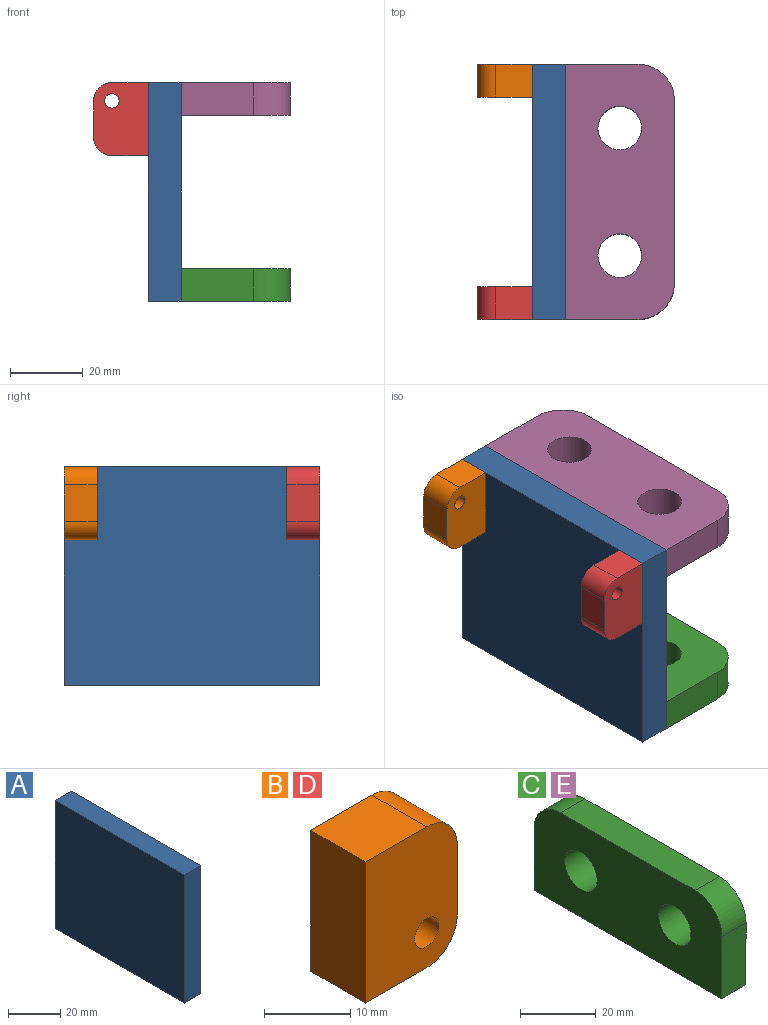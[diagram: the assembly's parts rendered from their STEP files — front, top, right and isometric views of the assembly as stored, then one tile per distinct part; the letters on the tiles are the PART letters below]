
ASSEMBLY  parts=5 mates=12
PART A: 6 faces, bbox 9x70x60 mm
  f0: plane 70x60mm, normal (1,0,0), area 4200mm2, adj f1,f2,f4,f5
  f1: plane 70x9mm, normal (0,0,1), area 630mm2, adj f0,f3,f4,f5
  f2: plane 70x9mm, normal (0,0,-1), area 630mm2, adj f0,f3,f4,f5
  f3: plane 70x60mm, normal (-1,0,0), area 4200mm2, adj f1,f2,f4,f5
  f4: plane 60x9mm, normal (0,1,0), area 540mm2, adj f0,f1,f2,f3
  f5: plane 60x9mm, normal (0,-1,0), area 540mm2, adj f0,f1,f2,f3
PART B: 9 faces, bbox 15x9x20 mm
  f0: plane 10x9mm, normal (0,0,-1), area 90mm2, adj f1,f2,f4,f7
  f1: plane 20x15mm, normal (0,-1,0), area 276.7mm2, adj f0,f3,f4,f5,f6,f7,f8
  f2: plane 20x15mm, normal (0,1,0), area 276.7mm2, adj f0,f3,f4,f5,f6,f7,f8
  f3: plane 10x9mm, normal (0,0,1), area 90mm2, adj f1,f2,f4,f8
  f4: plane 20x9mm, normal (-1,0,0), area 180mm2, adj f0,f1,f2,f3
  f5: cylinder r=2mm len=9mm, axis (0,1,0), area 113.1mm2, adj f1,f2
  f6: plane 10x9mm, normal (1,0,0), area 90mm2, adj f1,f2,f7,f8
  f7: cylinder r=5mm len=9mm, axis (0,1,0), area 70.7mm2, adj f0,f1,f2,f6
  f8: cylinder r=5mm len=9mm, axis (0,-1,0), area 70.7mm2, adj f1,f2,f3,f6
PART C: 10 faces, bbox 9x70x30 mm
  f0: cylinder r=10mm len=10mm, axis (-1,0,0), area 141.4mm2, adj f1,f5,f8,f9
  f1: plane 50x9mm, normal (0,0,1), area 450mm2, adj f0,f2,f8,f9
  f2: cylinder r=10mm len=10mm, axis (-1,0,0), area 141.4mm2, adj f1,f3,f8,f9
  f3: plane 20x9mm, normal (0,-1,0), area 180mm2, adj f2,f4,f8,f9
  f4: plane 70x9mm, normal (0,0,-1), area 630mm2, adj f3,f5,f8,f9
  f5: plane 20x9mm, normal (0,1,0), area 180mm2, adj f0,f4,f8,f9
  f6: cylinder r=6mm len=12mm, axis (-1,0,0), area 339.3mm2, adj f8,f9
  f7: cylinder r=6mm len=12mm, axis (-1,0,0), area 339.3mm2, adj f8,f9
  f8: plane 70x30mm, normal (1,0,0), area 1830.9mm2, adj f0,f1,f2,f3,f4,f5,f6,f7
  f9: plane 70x30mm, normal (-1,0,0), area 1830.9mm2, adj f0,f1,f2,f3,f4,f5,f6,f7
PART D: same geometry as B
PART E: same geometry as C
PLACE A t=(-24.72,-25.45,9.34)mm fixed
PLACE B rot(axis=(0,1,0),180deg) t=(-24.72,49.55,69.34)mm
PLACE C rot(axis=(0,1,0),90deg) t=(-15.72,-20.45,18.34)mm
PLACE D rot(axis=(0,1,0),180deg) t=(-24.72,-11.45,69.34)mm
PLACE E rot(axis=(0.71,0,0.71),180deg) t=(-15.72,49.55,60.34)mm
MATE planar E.f4 <-> A.f0  axis (-1,0,0) through (-15.72,49.55,69.34)mm
MATE planar C.f8 <-> A.f2  axis (0,0,-1) through (-1.02,14.55,9.34)mm
MATE planar A.f1 <-> B.f0  axis (0,0,1) through (-24.72,49.55,69.34)mm
MATE planar D.f4 <-> A.f3  axis (1,0,0) through (-24.72,-15.95,59.34)mm
MATE planar A.f1 <-> D.f0  axis (0,0,1) through (-20.22,14.55,69.34)mm
MATE planar B.f2 <-> A.f4  axis (0,1,0) through (-31.86,49.55,59.11)mm
MATE planar C.f3 <-> A.f5  axis (0,-1,0) through (-5.72,-20.45,13.84)mm
MATE planar B.f4 <-> A.f3  axis (1,0,0) through (-24.72,45.05,59.34)mm
MATE planar A.f0 <-> C.f4  axis (1,0,0) through (-15.72,14.55,39.34)mm
MATE planar A.f5 <-> D.f1  axis (0,-1,0) through (-20.22,-20.45,39.34)mm
MATE planar E.f3 <-> A.f4  axis (0,1,0) through (-5.72,49.55,64.84)mm
MATE planar E.f8 <-> A.f1  axis (0,0,1) through (-1.02,14.55,69.34)mm
